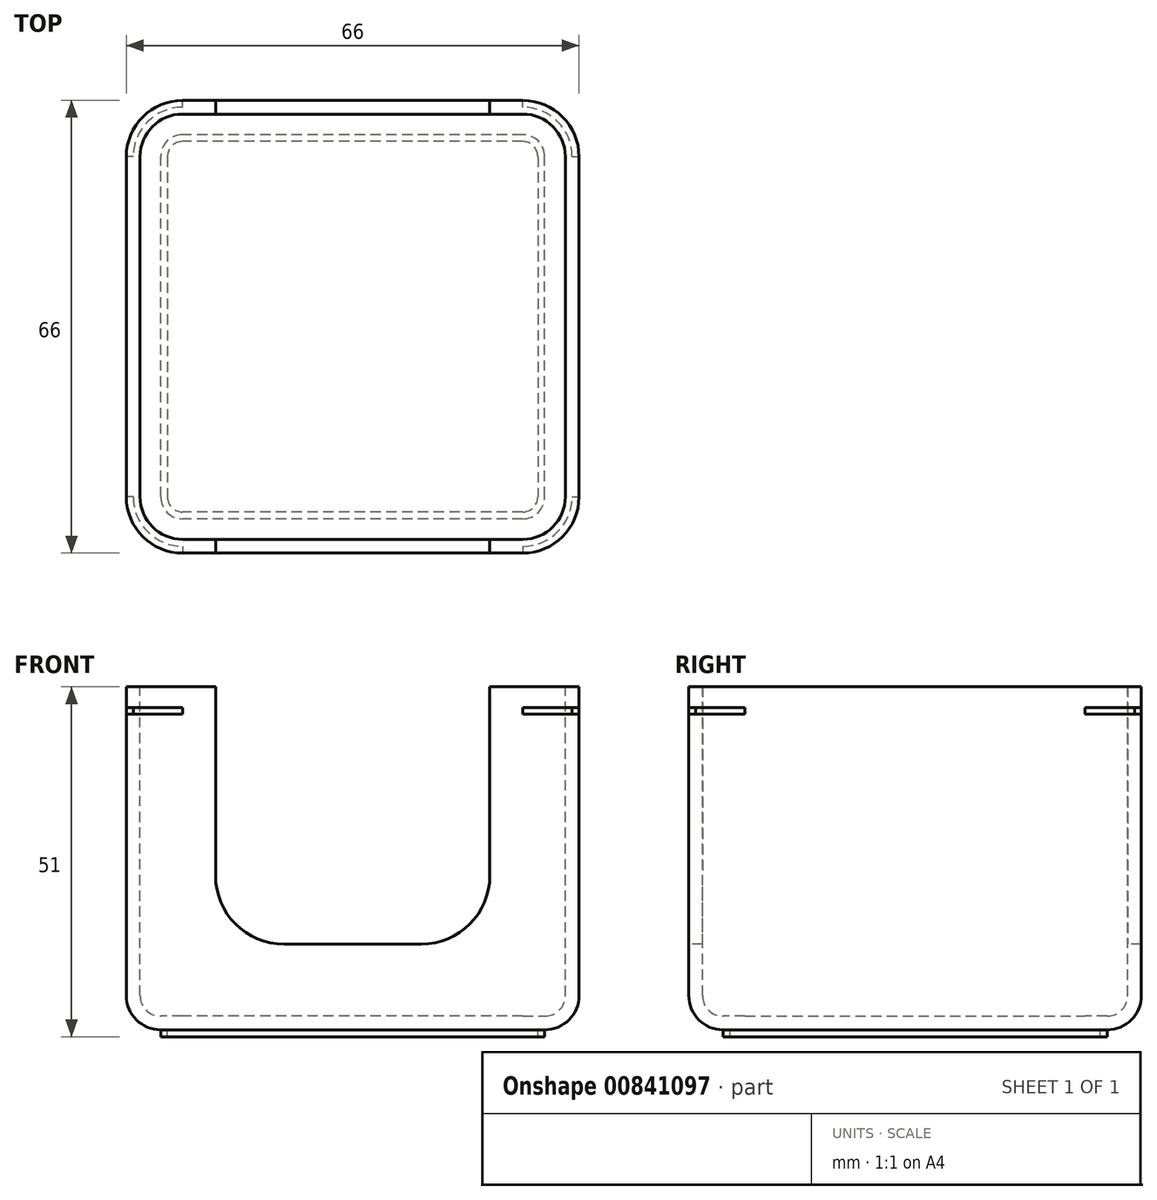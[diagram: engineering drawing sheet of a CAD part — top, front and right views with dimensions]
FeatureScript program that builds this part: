
annotation { "Feature Type Name" : "Feature", "Feature Type Description" : "" }
export const myFeature = defineFeature(function(context is Context, id is Id, definition is map)
    precondition{}
    {
        {
            var Q0;
            Q0=qCreatedBy(makeId("Top.planeOp"),FACE);
            var sketch = newSketch(context, id + "F0", { "sketchPlane" : qUnion([Q0])});
            skLineSegment(sketch, "E0.bottom", {"start": v(24.8, -33) * mm, "end": v(-24.8, -33) * mm});
            skLineSegment(sketch, "E0.top", {"start": v(24.8, 33) * mm, "end": v(-24.8, 33) * mm});
            skLineSegment(sketch, "E0.left", {"start": v(33, -24.8) * mm, "end": v(33, 24.8) * mm});
            skLineSegment(sketch, "E0.right", {"start": v(-33, -24.8) * mm, "end": v(-33, 24.8) * mm});
            skPoint(sketch, "E0.middle", {"position": v(0, 0) * mm});
            skPoint(sketch, "E1.visualSharp", {"position": v(-33, 33) * mm});
            skArc(sketch, "E1.filletArc", {"start": v(-24.8, 33) * mm, "mid": v(-30.6, 30.6) * mm, "end": v(-33, 24.8) * mm});
            skPoint(sketch, "E2.visualSharp", {"position": v(33, 33) * mm});
            skArc(sketch, "E2.filletArc", {"start": v(33, 24.8) * mm, "mid": v(30.6, 30.6) * mm, "end": v(24.8, 33) * mm});
            skPoint(sketch, "E3.visualSharp", {"position": v(33, -33) * mm});
            skArc(sketch, "E3.filletArc", {"start": v(24.8, -33) * mm, "mid": v(30.6, -30.6) * mm, "end": v(33, -24.8) * mm});
            skPoint(sketch, "E4.visualSharp", {"position": v(-33, -33) * mm});
            skArc(sketch, "E4.filletArc", {"start": v(-33, -24.8) * mm, "mid": v(-30.6, -30.6) * mm, "end": v(-24.8, -33) * mm});
            skSolve(sketch);
        }
        {
            var Q0;
            Q0 = qSketchRegion(id + "F0", true);
            extrude(context, id + "F1", {"entities" : qUnion([Q0]), "oppositeDirection" : true, "depth" : 50 * mm, "offsetDistance" : 25 * mm});
        }
        {
            var Q0;
            Q0=makeQuery(id+"F1.opExtrude","CAP_EDGE",EDGE,{"disambiguationData":[OSD([sQuery(id+"F0.wireOp",EDGE,"E0.bottom")])],"isStart":false});
            fillet(context, id + "F2", {"entities" : qUnion([Q0]), "radius" : 5 * mm, "tangentPropagation" : true, "allowEdgeOverflow" : false});
        }
        {
            var Q0;
            Q0=makeQuery(id+"F1.opExtrude","CAP_FACE",FACE,{"disambiguationData":[OSD([sQuery(id+"F0.wireOp",EDGE,"E0.bottom"),sQuery(id+"F0.wireOp",EDGE,"E0.top"),sQuery(id+"F0.wireOp",EDGE,"E0.left"),sQuery(id+"F0.wireOp",EDGE,"E0.right"),sQuery(id+"F0.wireOp",EDGE,"E1.filletArc"),sQuery(id+"F0.wireOp",EDGE,"E2.filletArc"),sQuery(id+"F0.wireOp",EDGE,"E3.filletArc"),sQuery(id+"F0.wireOp",EDGE,"E4.filletArc")])],"isStart":false});
            var sketch = newSketch(context, id + "F3", { "sketchPlane" : qUnion([Q0])});
            skLineSegment(sketch, "E5.bottom", {"start": v(24.8, -28) * mm, "end": v(-24.8, -28) * mm});
            skLineSegment(sketch, "E5.top", {"start": v(24.8, 28) * mm, "end": v(-24.8, 28) * mm});
            skLineSegment(sketch, "E5.left", {"start": v(28, -24.8) * mm, "end": v(28, 24.8) * mm});
            skLineSegment(sketch, "E5.right", {"start": v(-28, -24.8) * mm, "end": v(-28, 24.8) * mm});
            skPoint(sketch, "E5.middle", {"position": v(0, 0) * mm});
            skPoint(sketch, "E6.visualSharp", {"position": v(28, 28) * mm});
            skArc(sketch, "E6.filletArc", {"start": v(28, 24.8) * mm, "mid": v(27.06, 27.06) * mm, "end": v(24.8, 28) * mm});
            skPoint(sketch, "E7.visualSharp", {"position": v(28, -28) * mm});
            skArc(sketch, "E7.filletArc", {"start": v(24.8, -28) * mm, "mid": v(27.06, -27.06) * mm, "end": v(28, -24.8) * mm});
            skPoint(sketch, "E8.visualSharp", {"position": v(-28, -28) * mm});
            skArc(sketch, "E8.filletArc", {"start": v(-28, -24.8) * mm, "mid": v(-27.06, -27.06) * mm, "end": v(-24.8, -28) * mm});
            skPoint(sketch, "E9.visualSharp", {"position": v(-28, 28) * mm});
            skArc(sketch, "E9.filletArc", {"start": v(-24.8, 28) * mm, "mid": v(-27.06, 27.06) * mm, "end": v(-28, 24.8) * mm});
            skArc(sketch, "E10.0", {"start": v(27, 24.8) * mm, "mid": v(26.36, 26.36) * mm, "end": v(24.8, 27) * mm});
            skLineSegment(sketch, "E10.1", {"start": v(27, -24.8) * mm, "end": v(27, 24.8) * mm});
            skLineSegment(sketch, "E10.2", {"start": v(24.8, 27) * mm, "end": v(-24.8, 27) * mm});
            skArc(sketch, "E10.3", {"start": v(24.8, -27) * mm, "mid": v(26.36, -26.36) * mm, "end": v(27, -24.8) * mm});
            skArc(sketch, "E10.4", {"start": v(-24.8, 27) * mm, "mid": v(-26.36, 26.36) * mm, "end": v(-27, 24.8) * mm});
            skLineSegment(sketch, "E10.5", {"start": v(-27, -24.8) * mm, "end": v(-27, 24.8) * mm});
            skArc(sketch, "E10.6", {"start": v(-27, -24.8) * mm, "mid": v(-26.36, -26.36) * mm, "end": v(-24.8, -27) * mm});
            skLineSegment(sketch, "E10.7", {"start": v(24.8, -27) * mm, "end": v(-24.8, -27) * mm});
            skSolve(sketch);
        }
        {
            var Q0;
            Q0 = qSketchRegion(id + "F3", true);
            extrude(context, id + "F4", {"entities" : qUnion([Q0]), "operationType" : NewBodyOperationType.ADD, "depth" : 1 * mm, "offsetDistance" : 25 * mm});
        }
        {
            var Q0;
            Q0=makeQuery(id+"F1.opExtrude","CAP_FACE",FACE,{"disambiguationData":[OSD([sQuery(id+"F0.wireOp",EDGE,"E0.bottom"),sQuery(id+"F0.wireOp",EDGE,"E0.top"),sQuery(id+"F0.wireOp",EDGE,"E0.left"),sQuery(id+"F0.wireOp",EDGE,"E0.right"),sQuery(id+"F0.wireOp",EDGE,"E1.filletArc"),sQuery(id+"F0.wireOp",EDGE,"E2.filletArc"),sQuery(id+"F0.wireOp",EDGE,"E3.filletArc"),sQuery(id+"F0.wireOp",EDGE,"E4.filletArc")])],"isStart":true});
            shell(context, id + "F5", {"entities" : qUnion([Q0]), "thickness" : 2 * mm});
        }
        {
            var Q0;
            Q0=qCreatedBy(makeId("Top.planeOp"),FACE);
            cPlane(context, id + "F6", {"entities" : qUnion([Q0]), "cplaneType" : CPlaneType.OFFSET, "offset" : 3 * mm, "oppositeDirection" : true, "width" : 150 * mm, "height" : 150 * mm});
        }
        {
            var Q0;
            Q0=qCreatedBy(id+"F6.planeOp",FACE);
            var sketch = newSketch(context, id + "F7", { "sketchPlane" : qUnion([Q0])});
            skArc(sketch, "E11", {"start": v(24.8, -33) * mm, "mid": v(30.6, -30.6) * mm, "end": v(33, -24.8) * mm});
            skArc(sketch, "E12.0", {"start": v(24.8, -32) * mm, "mid": v(29.9, -29.9) * mm, "end": v(32, -24.8) * mm});
            skLineSegment(sketch, "E13", {"start": v(32, -24.8) * mm, "end": v(33, -24.8) * mm});
            skLineSegment(sketch, "E14", {"start": v(24.8, -32) * mm, "end": v(24.8, -33) * mm});
            skArc(sketch, "E15.1.0", {"start": v(32, 24.8) * mm, "mid": v(29.9, 29.9) * mm, "end": v(24.8, 32) * mm});
            skArc(sketch, "E15.1.1", {"start": v(33, 24.8) * mm, "mid": v(30.6, 30.6) * mm, "end": v(24.8, 33) * mm});
            skLineSegment(sketch, "E15.1.2", {"start": v(32, 24.8) * mm, "end": v(33, 24.8) * mm});
            skLineSegment(sketch, "E15.1.3", {"start": v(24.8, 32) * mm, "end": v(24.8, 33) * mm});
            skArc(sketch, "E15.2.0", {"start": v(-24.8, 32) * mm, "mid": v(-29.9, 29.9) * mm, "end": v(-32, 24.8) * mm});
            skArc(sketch, "E15.2.1", {"start": v(-24.8, 33) * mm, "mid": v(-30.6, 30.6) * mm, "end": v(-33, 24.8) * mm});
            skLineSegment(sketch, "E15.2.2", {"start": v(-24.8, 32) * mm, "end": v(-24.8, 33) * mm});
            skLineSegment(sketch, "E15.2.3", {"start": v(-32, 24.8) * mm, "end": v(-33, 24.8) * mm});
            skArc(sketch, "E15.3.0", {"start": v(-32, -24.8) * mm, "mid": v(-29.9, -29.9) * mm, "end": v(-24.8, -32) * mm});
            skArc(sketch, "E15.3.1", {"start": v(-33, -24.8) * mm, "mid": v(-30.6, -30.6) * mm, "end": v(-24.8, -33) * mm});
            skLineSegment(sketch, "E15.3.2", {"start": v(-32, -24.8) * mm, "end": v(-33, -24.8) * mm});
            skLineSegment(sketch, "E15.3.3", {"start": v(-24.8, -32) * mm, "end": v(-24.8, -33) * mm});
            skPoint(sketch, "E15.center", {"position": v(0, 0) * mm});
            skSolve(sketch);
        }
        {
            var Q0;
            Q0 = qSketchRegion(id + "F7", true);
            extrude(context, id + "F8", {"entities" : qUnion([Q0]), "operationType" : NewBodyOperationType.REMOVE, "oppositeDirection" : true, "depth" : 1 * mm, "offsetDistance" : 25 * mm});
        }
        {
            var Q0;
            Q0=qCreatedBy(makeId("Front.planeOp"),FACE);
            var sketch = newSketch(context, id + "F9", { "sketchPlane" : qUnion([Q0])});
            skLineSegment(sketch, "E16", {"start": v(0, 0) * mm, "end": v(0, 11.9) * mm});
            skSolve(sketch);
        }
        {
            var Q0;
            Q0=makeQuery(id+"F1.opExtrude","SWEPT_BODY",BODY,{"disambiguationData":[OSD([sQuery(id+"F0.wireOp",EDGE,"E0.bottom"),sQuery(id+"F0.wireOp",EDGE,"E0.top"),sQuery(id+"F0.wireOp",EDGE,"E0.left"),sQuery(id+"F0.wireOp",EDGE,"E0.right"),sQuery(id+"F0.wireOp",EDGE,"E1.filletArc"),sQuery(id+"F0.wireOp",EDGE,"E2.filletArc"),sQuery(id+"F0.wireOp",EDGE,"E3.filletArc"),sQuery(id+"F0.wireOp",EDGE,"E4.filletArc")])]});
            var Q1;
            Q1=sQuery(id+"F9.wireOp",EDGE,"E16");
            circularPattern(context, id + "F10", {"entities" : qUnion([Q0]), "axis" : qUnion([Q1]), "angle" : 360 * degree, "instanceCount" : 4, "equalSpace" : true});
        }
        {
            var Q0;
            Q0=makeQuery(id+"F1.opExtrude","SWEPT_FACE",FACE,{"disambiguationData":[OSD([sQuery(id+"F0.wireOp",EDGE,"E0.bottom")])]});
            var sketch = newSketch(context, id + "F11", { "sketchPlane" : qUnion([Q0])});
            skLineSegment(sketch, "E17.bottom", {"start": v(10, -37.5) * mm, "end": v(-10, -37.5) * mm});
            skLineSegment(sketch, "E17.left", {"start": v(20, -27.5) * mm, "end": v(20, 0) * mm});
            skLineSegment(sketch, "E17.right", {"start": v(-20, -27.5) * mm, "end": v(-20, 0) * mm});
            skPoint(sketch, "E17.middle", {"position": v(0, 0) * mm});
            skPoint(sketch, "E18.visualSharp", {"position": v(-20, -37.5) * mm});
            skArc(sketch, "E18.filletArc", {"start": v(-20, -27.5) * mm, "mid": v(-17.07, -34.57) * mm, "end": v(-10, -37.5) * mm});
            skPoint(sketch, "E19.visualSharp", {"position": v(20, -37.5) * mm});
            skArc(sketch, "E19.filletArc", {"start": v(10, -37.5) * mm, "mid": v(17.07, -34.57) * mm, "end": v(20, -27.5) * mm});
            skLineSegment(sketch, "E20", {"start": v(0, 0) * mm, "end": v(20, 0) * mm});
            skLineSegment(sketch, "E21", {"start": v(20, 0) * mm, "end": v(-20, 0) * mm});
            skSolve(sketch);
        }
        {
            var Q0;
            Q0 = qSketchRegion(id + "F11", true);
            extrude(context, id + "F12", {"entities" : qUnion([Q0]), "operationType" : NewBodyOperationType.REMOVE, "endBound" : BoundingType.THROUGH_ALL, "oppositeDirection" : true, "depth" : 25 * mm, "offsetDistance" : 25 * mm});
        }
        {
            var Q0;
            Q0=makeQuery(id+"F10.opPattern","COPY",BODY,{"derivedFrom":makeQuery(id+"F1.opExtrude","SWEPT_BODY",BODY,{"disambiguationData":[OSD([sQuery(id+"F0.wireOp",EDGE,"E0.bottom"),sQuery(id+"F0.wireOp",EDGE,"E0.top"),sQuery(id+"F0.wireOp",EDGE,"E0.left"),sQuery(id+"F0.wireOp",EDGE,"E0.right"),sQuery(id+"F0.wireOp",EDGE,"E1.filletArc"),sQuery(id+"F0.wireOp",EDGE,"E2.filletArc"),sQuery(id+"F0.wireOp",EDGE,"E3.filletArc"),sQuery(id+"F0.wireOp",EDGE,"E4.filletArc")])]}),"instanceName":"1"});
            var Q1;
            Q1=makeQuery(id+"F10.opPattern","COPY",BODY,{"derivedFrom":makeQuery(id+"F1.opExtrude","SWEPT_BODY",BODY,{"disambiguationData":[OSD([sQuery(id+"F0.wireOp",EDGE,"E0.bottom"),sQuery(id+"F0.wireOp",EDGE,"E0.top"),sQuery(id+"F0.wireOp",EDGE,"E0.left"),sQuery(id+"F0.wireOp",EDGE,"E0.right"),sQuery(id+"F0.wireOp",EDGE,"E1.filletArc"),sQuery(id+"F0.wireOp",EDGE,"E2.filletArc"),sQuery(id+"F0.wireOp",EDGE,"E3.filletArc"),sQuery(id+"F0.wireOp",EDGE,"E4.filletArc")])]}),"instanceName":"2"});
            var Q2;
            Q2=makeQuery(id+"F10.opPattern","COPY",BODY,{"derivedFrom":makeQuery(id+"F1.opExtrude","SWEPT_BODY",BODY,{"disambiguationData":[OSD([sQuery(id+"F0.wireOp",EDGE,"E0.bottom"),sQuery(id+"F0.wireOp",EDGE,"E0.top"),sQuery(id+"F0.wireOp",EDGE,"E0.left"),sQuery(id+"F0.wireOp",EDGE,"E0.right"),sQuery(id+"F0.wireOp",EDGE,"E1.filletArc"),sQuery(id+"F0.wireOp",EDGE,"E2.filletArc"),sQuery(id+"F0.wireOp",EDGE,"E3.filletArc"),sQuery(id+"F0.wireOp",EDGE,"E4.filletArc")])]}),"instanceName":"3"});
            deleteBodies(context, id + "F13", {"entities" : qUnion([Q0, Q1, Q2])});
        }
    });
